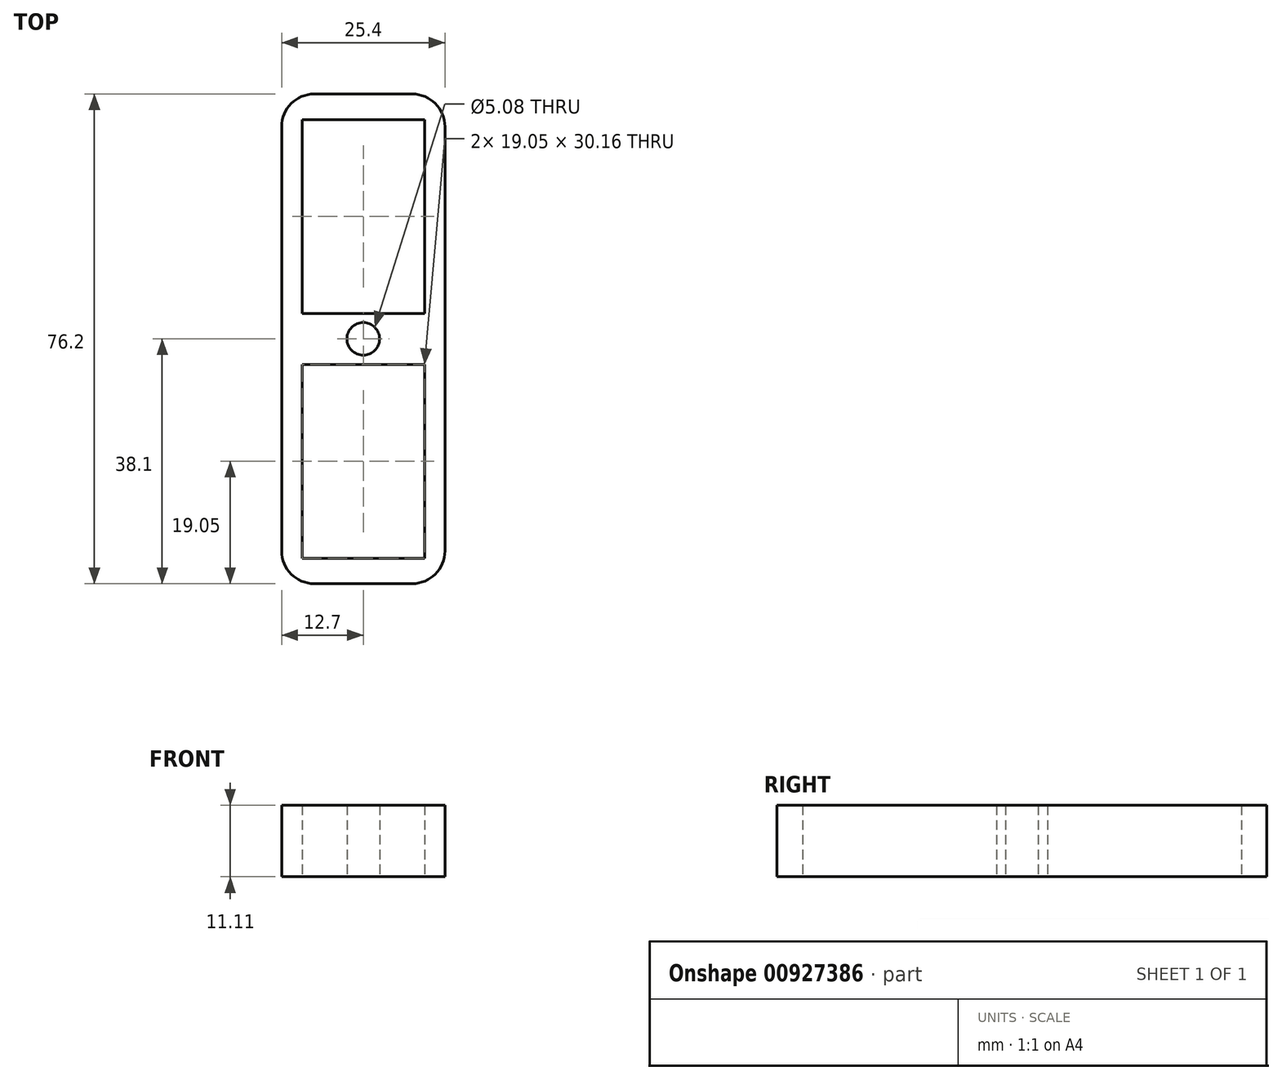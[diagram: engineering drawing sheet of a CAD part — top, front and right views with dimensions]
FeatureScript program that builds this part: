
annotation { "Feature Type Name" : "Feature", "Feature Type Description" : "" }
export const myFeature = defineFeature(function(context is Context, id is Id, definition is map)
    precondition{}
    {
        {
            var Q0;
            Q0=qCreatedBy(makeId("Top.planeOp"),FACE);
            var sketch = newSketch(context, id + "F0", { "sketchPlane" : qUnion([Q0])});
            skLineSegment(sketch, "E0.bottom", {"start": v(12.7, 38.1) * mm, "end": v(-12.7, 38.1) * mm});
            skLineSegment(sketch, "E0.top", {"start": v(12.7, -38.1) * mm, "end": v(-12.7, -38.1) * mm});
            skLineSegment(sketch, "E0.left", {"start": v(12.7, 38.1) * mm, "end": v(12.7, -38.1) * mm});
            skLineSegment(sketch, "E0.right", {"start": v(-12.7, 38.1) * mm, "end": v(-12.7, -38.1) * mm});
            skPoint(sketch, "E0.middle", {"position": v(0, 0) * mm});
            skLineSegment(sketch, "E1.bottom", {"start": v(9.53, 3.97) * mm, "end": v(-9.53, 3.97) * mm});
            skLineSegment(sketch, "E1.top", {"start": v(9.53, 34.13) * mm, "end": v(-9.53, 34.13) * mm});
            skLineSegment(sketch, "E1.left", {"start": v(9.53, 3.97) * mm, "end": v(9.53, 34.13) * mm});
            skLineSegment(sketch, "E1.right", {"start": v(-9.53, 3.97) * mm, "end": v(-9.53, 34.13) * mm});
            skPoint(sketch, "E1.middle", {"position": v(0, 19.05) * mm});
            skLineSegment(sketch, "E2.bottom", {"start": v(9.53, -3.97) * mm, "end": v(-9.53, -3.97) * mm});
            skLineSegment(sketch, "E2.top", {"start": v(9.52, -34.13) * mm, "end": v(-9.53, -34.13) * mm});
            skLineSegment(sketch, "E2.left", {"start": v(9.53, -3.97) * mm, "end": v(9.53, -34.13) * mm});
            skLineSegment(sketch, "E2.right", {"start": v(-9.53, -3.97) * mm, "end": v(-9.53, -34.13) * mm});
            skPoint(sketch, "E2.middle", {"position": v(0, -19.05) * mm});
            skCircle(sketch, "E3", {"center": v(0, 0) * mm, "radius": 2.54 * mm});
            skSolve(sketch);
        }
        {
            var Q0;
            Q0 = qSketchRegion(id + "F0", true);
            extrude(context, id + "F1", {"entities" : qUnion([Q0]), "depth" : 11.1 * mm, "offsetDistance" : 25.4 * mm});
        }
        {
            var Q0;
            Q0=makeQuery(id+"F1.opExtrude","SWEPT_EDGE",EDGE,{"disambiguationData":[OSD([sQuery(id+"F0.wireOp",EDGE,"E0.top"),sQuery(id+"F0.wireOp",EDGE,"E0.left")])]});
            var Q1;
            Q1=makeQuery(id+"F1.opExtrude","SWEPT_EDGE",EDGE,{"disambiguationData":[OSD([sQuery(id+"F0.wireOp",EDGE,"E0.top"),sQuery(id+"F0.wireOp",EDGE,"E0.right")])]});
            var Q2;
            Q2=makeQuery(id+"F1.opExtrude","SWEPT_EDGE",EDGE,{"disambiguationData":[OSD([sQuery(id+"F0.wireOp",EDGE,"E0.bottom"),sQuery(id+"F0.wireOp",EDGE,"E0.left")])]});
            var Q3;
            Q3=makeQuery(id+"F1.opExtrude","SWEPT_EDGE",EDGE,{"disambiguationData":[OSD([sQuery(id+"F0.wireOp",EDGE,"E0.bottom"),sQuery(id+"F0.wireOp",EDGE,"E0.right")])]});
            fillet(context, id + "F2", {"entities" : qUnion([Q0, Q1, Q2, Q3]), "radius" : 5.08 * mm, "tangentPropagation" : true, "allowEdgeOverflow" : false});
        }
    });
